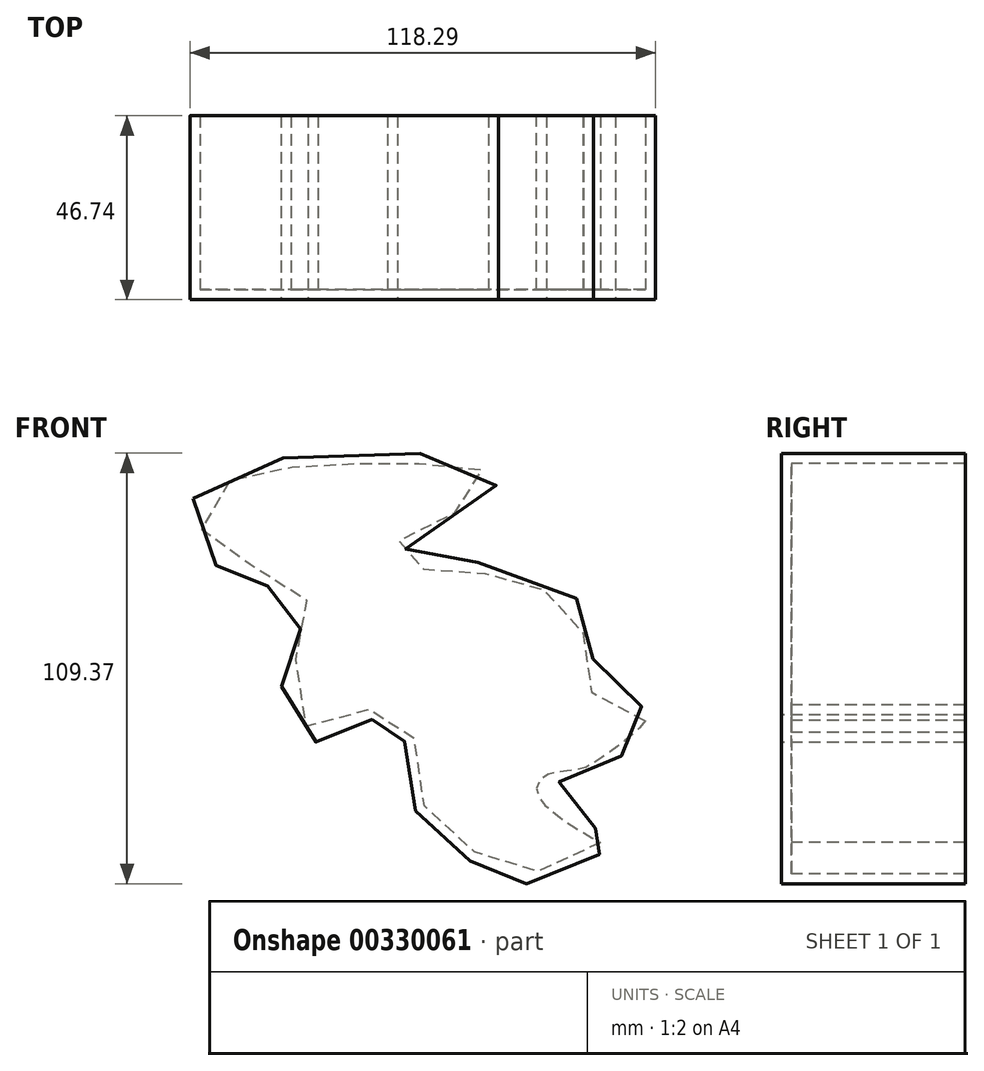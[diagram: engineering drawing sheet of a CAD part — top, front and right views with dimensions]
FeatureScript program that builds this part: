
annotation { "Feature Type Name" : "Feature", "Feature Type Description" : "" }
export const myFeature = defineFeature(function(context is Context, id is Id, definition is map)
    precondition{}
    {
        {
            var Q0;
            Q0=qCreatedBy(makeId("Front.planeOp"),FACE);
            var sketch = newSketch(context, id + "F0", { "sketchPlane" : qUnion([Q0])});
            skFitSpline(sketch, "E0", {"points": [v(-66.6, 36.48) * mm, v(-50.6, 45.65) * mm, v(-14.35, 48) * mm, v(10.82, 43.77) * mm, v(0, 29.89) * mm, v(-14.6, 22.12) * mm, v(12.47, 19.3) * mm, v(30.6, 11.3) * mm, v(34.36, 6.82) * mm, v(35.06, -4.7) * mm, v(36.95, -11.3) * mm, v(50.36, -18.36) * mm, v(49.18, -23.06) * mm, v(37.42, -32.24) * mm, v(31.53, -34.83) * mm, v(23.3, -37.18) * mm, v(35.3, -47.06) * mm, v(39.3, -49.42) * mm, v(40.71, -51.07) * mm, v(34.6, -54.83) * mm, v(21.65, -60.71) * mm, v(14.35, -60.95) * mm, v(7.53, -57.65) * mm, v(-2.82, -51.07) * mm, v(-9.88, -43.06) * mm, v(-12.24, -36.48) * mm, v(-12.94, -23.06) * mm, v(-14.12, -19.06) * mm, v(-19.77, -19.06) * mm, v(-27.77, -23.77) * mm, v(-34.36, -25.41) * mm, v(-39.53, -23.3) * mm, v(-44, -11.3) * mm, v(-43.77, -6.82) * mm, v(-39.77, 2.82) * mm, v(-37.42, 6.59) * mm, v(-47.06, 13.88) * mm, v(-50.6, 16.47) * mm, v(-58.6, 18.83) * mm, v(-64.48, 22.6) * mm, v(-66.6, 36.48) * mm]});
            skSolve(sketch);
        }
        {
            var Q0;
            Q0=makeQuery(id+"F0.imprint","IMPRINT",FACE,{"disambiguationData":[TD([[makeQuery(id+"F0.imprint","IMPRINT",EDGE,{"derivedFrom":sQuery(id+"F0.wireOp",EDGE,"E0")}),-1.0]])]});
            extrude(context, id + "F1", {"entities" : qUnion([Q0]), "oppositeDirection" : true, "depth" : 46.74 * mm});
        }
        {
            var Q0;
            Q0=makeQuery(id+"F1.opExtrude","CAP_FACE",FACE,{"disambiguationData":[OSD([sQuery(id+"F0.wireOp",EDGE,"E0")])],"isStart":false});
            shell(context, id + "F2", {"entities" : qUnion([Q0]), "thickness" : 2.54 * mm});
        }
    });
